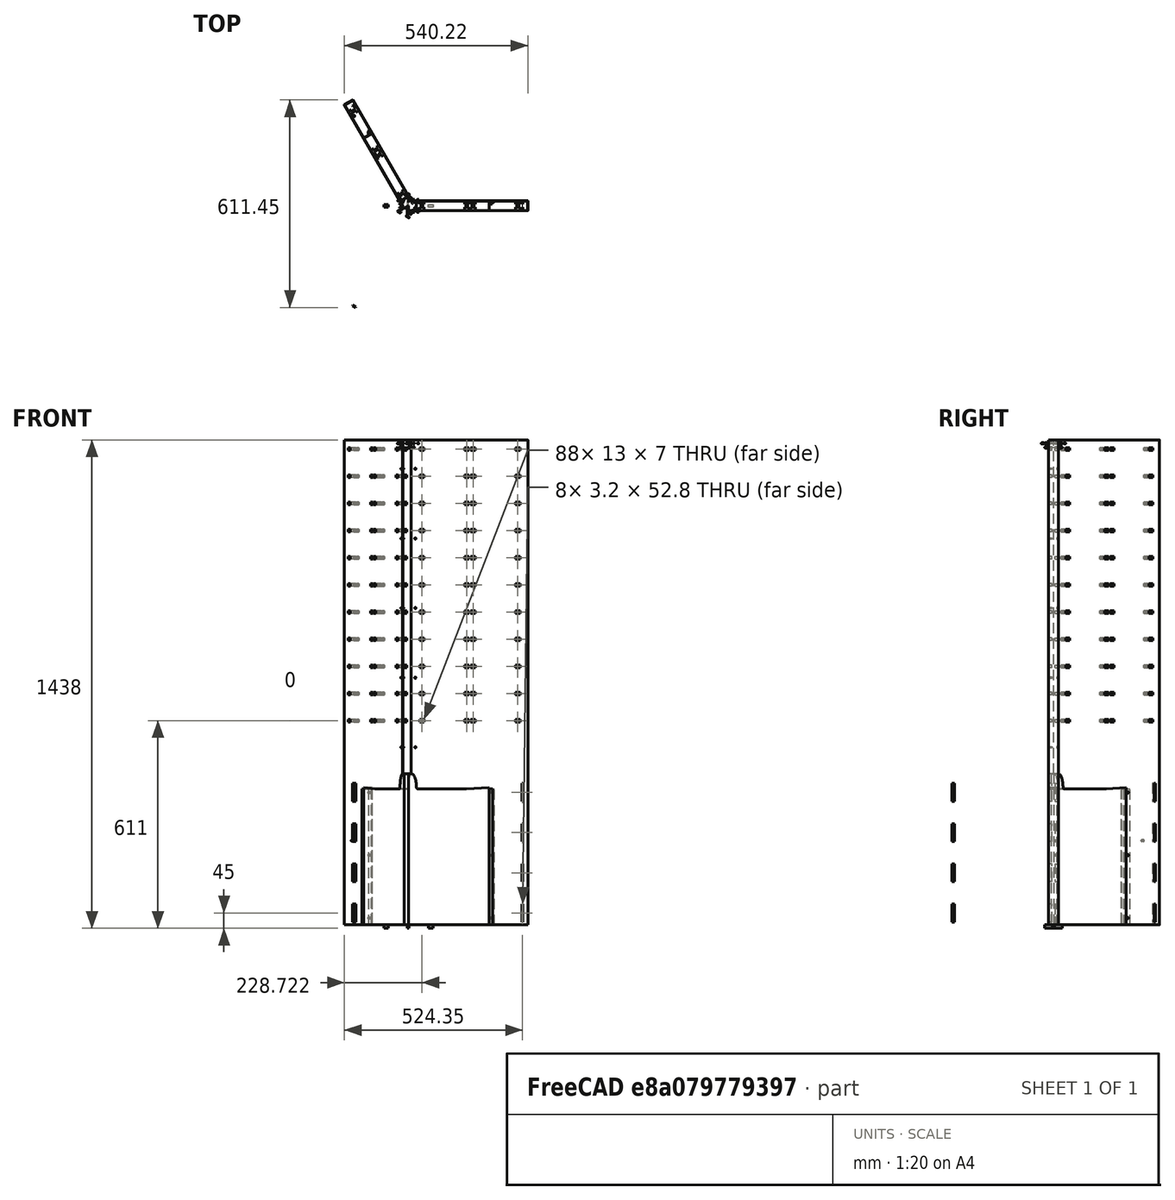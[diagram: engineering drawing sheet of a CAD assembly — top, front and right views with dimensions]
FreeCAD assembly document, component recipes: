
FREECAD ASSEMBLY — COMPONENT RECIPES ("composit_stand3_base_part2_model")

This assembly document has 4 components, labeled P0..P3 below (a component is one placed body or linked part). 3 of them carry a construction recipe — the FreeCAD feature program that regenerates the part from scratch, quoted from this document or its linked companion documents; the rest are supplied as boundary geometry only. No exploded tour is included for this assembly.
COMPONENT P0 — recipe-attached ("part2", modeled in this document).
Construction recipe (the document's own serialized feature program — sketch geometry with constraints, then the solid features built on it; lengths are millimeters unless a unit is written):

FEATURE [PartDesign::SubShapeBinder] Binder001
  BindCopyOnChange = 0
  BindMode = 0
  ClaimChildren = true
  Context = -> Body [Binder001.]
  Fuse = false
  MakeFace = true
  OffsetFill = false
  OffsetIntersection = false
  OffsetJoinType = 0
  OffsetOpenResult = false
  PartialLoad = false
  Relative = false
  Support = -> [Connect]
  _Version = 2
FEATURE [PartDesign::FeaturePython] BaseBend  # WARN: FeaturePython — macro-defined, semantics opaque (R4)
  BendSide = 0
  BendSketch = -> Binder001
  MidPlane = false
  Reverse = false
  Suppressed = false
  length = 1428
  radius = 0.1
  thickness = 0.3
  expr: length = composit_stand3_base_part1_main#<<top_placement>>.Placement.Base.z
FEATURE [PartDesign::CoordinateSystem] Local_CS  label="base_LCS"
  AttacherType = Attacher::AttachEngine3D
  AttachmentSupport = -> [XY_Plane]
  MapMode = 5
FEATURE [PartDesign::CoordinateSystem] Local_CS001  label="sink1_LCS"
  AttacherType = Attacher::AttachEngine3D
  AttachmentOffset = pos=(8.37158,14.5,410) rot=(0,0,1;1.0472rad)
  AttachmentSupport = -> [XY_Plane]
  MapMode = 5
  Placement = pos=(8.37158,14.5,410) rot=(0,0,1;1.0472rad)
  expr: AttachmentOffset = <<sink_placement>>.LinkedObject.Placement
FEATURE [PartDesign::CoordinateSystem] Local_CS002  label="sink2_LCS"
  AttacherType = Attacher::AttachEngine3D
  AttachmentOffset = pos=(-16.7432,7.1e-15,410) rot=(0,0,1;3.14159rad)
  AttachmentSupport = -> [XY_Plane]
  MapMode = 5
  Placement = pos=(-16.7432,7.1e-15,410) rot=(0,0,1;3.14159rad)
  expr: AttachmentOffset = placement(vector(0; 0; 0); rotation(120; 0; 0)) * <<sink1_LCS>>.AttachmentOffset
FEATURE [PartDesign::CoordinateSystem] Local_CS003  label="sink3_LCS"
  AttacherType = Attacher::AttachEngine3D
  AttachmentOffset = pos=(8.37158,-14.5,410) rot=(0,0,1;5.23599rad)
  AttachmentSupport = -> [XY_Plane]
  MapMode = 5
  Placement = pos=(8.37158,-14.5,410) rot=(0,0,1;5.23599rad)
  expr: AttachmentOffset = placement(vector(0; 0; 0); rotation(240; 0; 0)) * <<sink1_LCS>>.AttachmentOffset
FEATURE [PartDesign::CoordinateSystem] Local_CS004  label="top_LCS"
  AttacherType = Attacher::AttachEngine3D
  AttachmentOffset = pos=(0,0,1428) rot=(0,0,1;0rad)
  AttachmentSupport = -> [XY_Plane]
  MapMode = 5
  Placement = pos=(0,0,1428) rot=(0,0,1;0rad)
  expr: .AttachmentOffset.Base.z = <<BaseBend>>.length
FEATURE [PartDesign::CoordinateSystem] Local_CS005  label="top_LCS001"
  AttacherType = Attacher::AttachEngine3D
  AttachmentOffset = pos=(0,0,1428) rot=(0,0,1;2.0944rad)
  AttachmentSupport = -> [XY_Plane]
  MapMode = 5
  Placement = pos=(0,0,1428) rot=(0,0,1;2.0944rad)
  expr: .AttachmentOffset.Base.z = <<BaseBend>>.length
FEATURE [PartDesign::CoordinateSystem] Local_CS006  label="top_amplifier1_LCS"
  AttacherType = Attacher::AttachEngine3D
  AttachmentOffset = pos=(6.63953,11.5,1428) rot=(0,0,1;1.0472rad)
  AttachmentSupport = -> [XY_Plane]
  MapMode = 5
  Placement = pos=(6.63953,11.5,1428) rot=(0,0,1;1.0472rad)
  expr: AttachmentOffset = placement(vector(0; 0; <<BaseBend>>.length); rotation(60; 0; 0)) * placement(vector(<<composit_stand3_main>>#<<main_sketch>>.Constraints.corner_distance - 3 mm / sin(60); 0; 0); rotation(0; 0; 0))
FEATURE [PartDesign::CoordinateSystem] Local_CS007  label="top_amplifier2_LCS"
  AttacherType = Attacher::AttachEngine3D
  AttachmentOffset = pos=(-13.2791,6.2e-15,1428) rot=(0,0,1;3.14159rad)
  AttachmentSupport = -> [XY_Plane]
  MapMode = 5
  Placement = pos=(-13.2791,6.2e-15,1428) rot=(0,0,1;3.14159rad)
  expr: AttachmentOffset = placement(vector(0; 0; 0); rotation(120; 0; 0)) * <<top_amplifier1_LCS>>.AttachmentOffset
FEATURE [PartDesign::CoordinateSystem] Local_CS008  label="top_amplifier3_LCS"
  AttacherType = Attacher::AttachEngine3D
  AttachmentOffset = pos=(6.63953,-11.5,1428) rot=(0,0,1;5.23599rad)
  AttachmentSupport = -> [XY_Plane]
  MapMode = 5
  Placement = pos=(6.63953,-11.5,1428) rot=(0,0,1;5.23599rad)
  expr: AttachmentOffset = placement(vector(0; 0; 0); rotation(240; 0; 0)) * <<top_amplifier1_LCS>>.AttachmentOffset
FEATURE [PartDesign::Boolean] Boolean
  BaseFeature = -> BaseBend
  Group = -> [Fusion]
  Refine = true
  Suppressed = false
  Type = 1
  UsePlacement = true
FEATURE [PartDesign::Boolean] Boolean003
  BaseFeature = -> Boolean
  Group = -> [Fusion003]
  Refine = true
  Suppressed = false
  Type = 0
  UsePlacement = true
FEATURE [PartDesign::Body] Body  label="part2"
  AllowCompound = false
  Group = -> [Binder001,BaseBend,Local_CS,Local_CS001,Local_CS002,Local_CS003,Boolean,Local_CS004,Local_CS005,Local_CS006,Local_CS007,Local_CS008,Boolean003]
  Origin = -> Origin
  Tip = -> Boolean003
COMPONENT P1 — recipe-attached ("Body002", modeled in this document).
Construction recipe (the document's own serialized feature program — sketch geometry with constraints, then the solid features built on it; lengths are millimeters unless a unit is written):

FEATURE [PartDesign::FeaturePython] BaseBend001  # WARN: FeaturePython — macro-defined, semantics opaque (R4)
  BendSide = 0
  BendSketch = -> Binder004
  MidPlane = false
  Reverse = false
  Suppressed = false
  length = 400
  radius = 0.1
  thickness = 0.3
  expr: radius = <<BaseBend>>.radius
  expr: thickness = <<BaseBend>>.thickness
FEATURE [PartDesign::Boolean] Boolean001
  BaseFeature = -> BaseBend001
  Group = -> [Fusion001]
  Suppressed = false
  Type = 1
  UsePlacement = true
FEATURE [PartDesign::Body] Body002
  AllowCompound = false
  Group = -> [BaseBend001,Boolean001]
  Origin = -> Origin002
  Tip = -> Boolean001
COMPONENT P2 — recipe-attached ("Body003", modeled in this document).
Construction recipe (the document's own serialized feature program — sketch geometry with constraints, then the solid features built on it; lengths are millimeters unless a unit is written):

FEATURE [PartDesign::FeaturePython] BaseBend002  # WARN: FeaturePython — macro-defined, semantics opaque (R4)
  BendSide = 1
  BendSketch = -> Part__Mirroring002
  MidPlane = false
  Reverse = false
  Suppressed = false
  length = 400
  radius = 0.1
  thickness = 0.3
  expr: length = <<BaseBend001>>.length
  expr: radius = <<BaseBend>>.radius
  expr: thickness = <<BaseBend>>.thickness
FEATURE [PartDesign::Boolean] Boolean002
  BaseFeature = -> BaseBend002
  Group = -> [Fusion002]
  Suppressed = false
  Type = 1
  UsePlacement = true
FEATURE [PartDesign::Body] Body003
  AllowCompound = false
  Group = -> [BaseBend002,Boolean002]
  Origin = -> Origin003
  Tip = -> Boolean002
COMPONENT P3 — geometry summary ("basin_cut"; no construction recipe available for this part):
  bounding box: 445.0 x 238.4 x 29.0 mm
  tessellated surface: 192 triangles
  volume: 2797471 mm^3 (91% of its bounding box)
  symmetry: mirror-symmetric across its y mid-plane
PROVENANCE & LICENSES
A FreeCAD (.FCStd) document from a public repository crawl; recipes are the document's own serialized feature recipes (and, for linked parts, companion documents' recipes).
License: as declared in the source repository (recorded in the dataset sidecar).
